# Revit family: Faucet-Lavatory-Spout-KOHLER-COMPONENTS-K-77966T
name_source: partatom
category: Plumbing Fixtures
revit_build: Autodesk Revit 2017 (Build: 20160225_1515(x64)
units: mm (PartAtom-declared; Revit-internal decimal feet)

## family parameters
Cut with Voids When Loaded = No
Host = Face
OmniClass Number = 23.31.11.00
OmniClass Title = Faucets
Part Type = Normal
Room Calculation Point = No
Round Connector Dimension = Use Diameter
Shared = No

## types (6) — shared parameters
ADA Compliant = No
Assembly Code = D2010
CW Connection = Yes
Cold Water Inlet = Cold Water Inlet
Date Modified = 08/31/2020
Default Elevation = 36"
Description = Yi Ting 8-inch washbasin faucet curve type high spout
Drain Included = Yes
Flow Rate = 0 GPM
HW Connection = Yes
Height = 14 1/8"
Hot Water Inlet = Hot Water Inlet
Length = 6 5/8"
Manufacturer = KOHLER Co.
Master Format 2014 = 22 41 39
Master Format 2014 Name = Residential Faucets, Supplies, and Trim
Material = Metal construction
Pressure = 0.00 psi
Product Documentation Link = https://files.kohler.com.cn
Product Name = Components
Product Page URL = https://www.kohler.com.cn
Spout Reach = 6 5/8"
URL = http://www.kohler.com.cn
Vent Connection = No
Waste Connection = No
Waste Water Outlet = Waste Water Outlet
WaterSense Certified = No
Width = 2 3/8"

## per-type parameters (varying)
| type | Finish | Model | Type |
| AF- Flange Gold | Kohler-Metal-AF-Flange_Gold | K-77966T-AF | 1 |
| BN- Roman Silver | Kohler-Metal-BN-Roman_Silver | K-77966T-BN | 2 |
| RGD- Rose Gold | Kohler-Metal-RGD-Rose_Gold | K-77966T-RGD | 3 |
| CP- Polished Chrome | Kohler-Metal-CP-Polished_Chrome | K-77966T-CP | 4 |
| TT- Titanium Silver | Kohler-Metal-TT-Titanium_Silver | K-77966T-TT | 5 |
| 2BL- Original Black | Kohler-Metal-2BL-Original_Black | K-77966T-2BL | 6 |

## geometry (parser evidence)
native form markers: Sweep x6
no freeform markers — native parametric forms only
